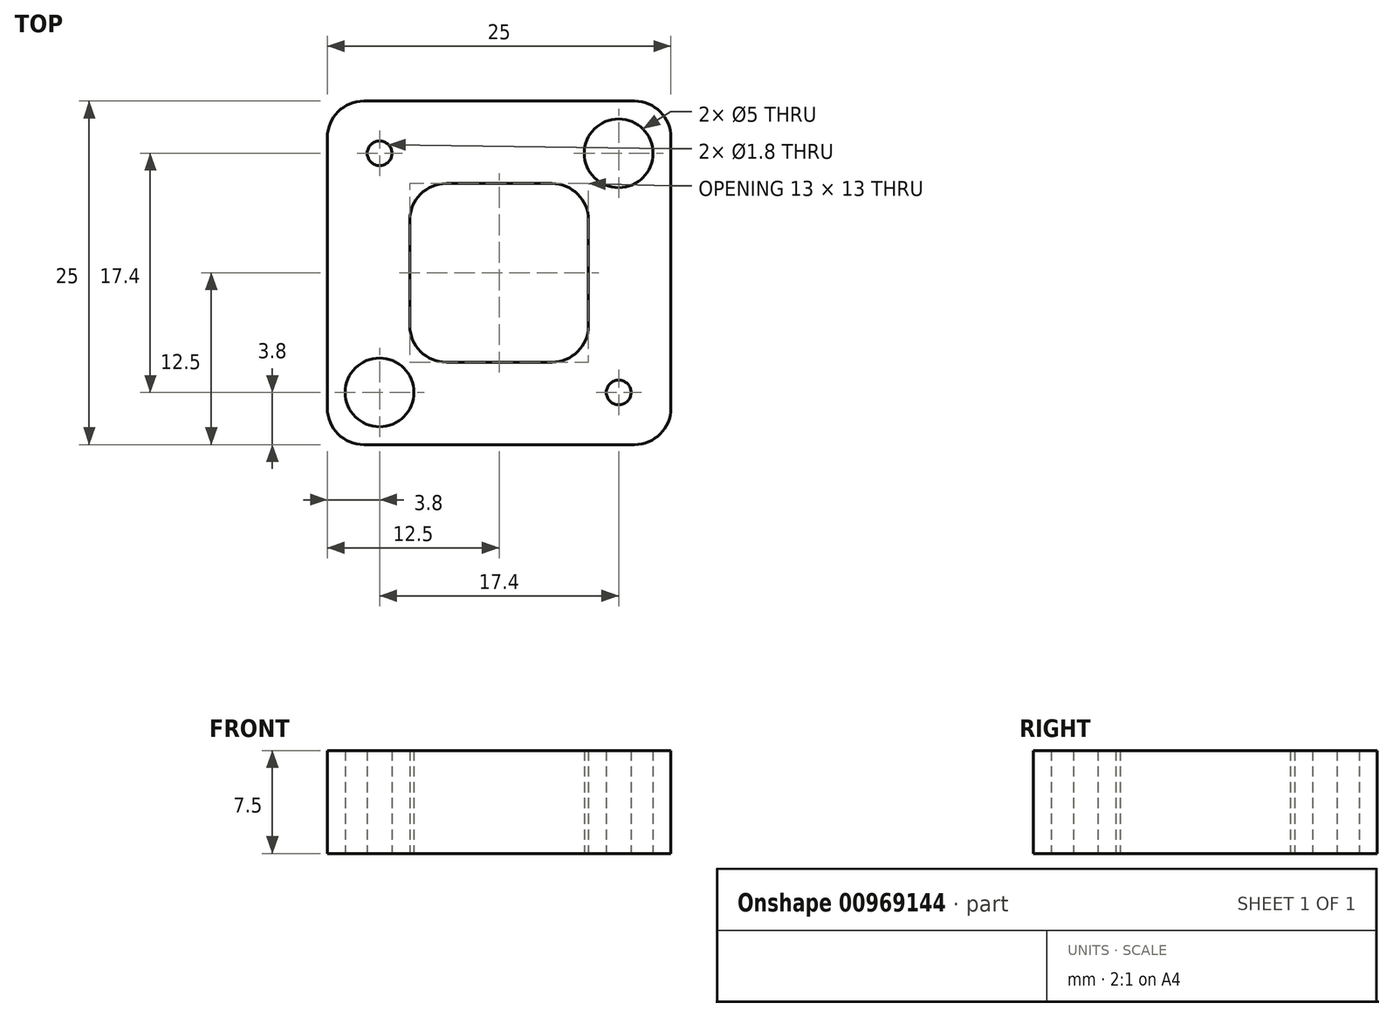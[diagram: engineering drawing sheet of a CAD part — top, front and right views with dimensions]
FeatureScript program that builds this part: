
annotation { "Feature Type Name" : "Feature", "Feature Type Description" : "" }
export const myFeature = defineFeature(function(context is Context, id is Id, definition is map)
    precondition{}
    {
        {
            var Q0;
            Q0=qCreatedBy(makeId("Top.planeOp"),FACE);
            var sketch = newSketch(context, id + "F0", { "sketchPlane" : qUnion([Q0])});
            skLineSegment(sketch, "E0.bottom", {"start": v(12.5, 12.5) * mm, "end": v(-12.5, 12.5) * mm});
            skLineSegment(sketch, "E0.top", {"start": v(12.5, -12.5) * mm, "end": v(-12.5, -12.5) * mm});
            skLineSegment(sketch, "E0.left", {"start": v(12.5, 12.5) * mm, "end": v(12.5, -12.5) * mm});
            skLineSegment(sketch, "E0.right", {"start": v(-12.5, 12.5) * mm, "end": v(-12.5, -12.5) * mm});
            skPoint(sketch, "E0.middle", {"position": v(0, 0) * mm});
            skLineSegment(sketch, "E1.bottom", {"start": v(6.5, 6.5) * mm, "end": v(-6.5, 6.5) * mm});
            skLineSegment(sketch, "E1.top", {"start": v(6.5, -6.5) * mm, "end": v(-6.5, -6.5) * mm});
            skLineSegment(sketch, "E1.left", {"start": v(6.5, 6.5) * mm, "end": v(6.5, -6.5) * mm});
            skLineSegment(sketch, "E1.right", {"start": v(-6.5, 6.5) * mm, "end": v(-6.5, -6.5) * mm});
            skCircle(sketch, "E2", {"center": v(-8.7, 8.7) * mm, "radius": 0.9 * mm});
            skCircle(sketch, "E3", {"center": v(-8.7, 8.7) * mm, "radius": 2.5 * mm});
            skLineSegment(sketch, "E4", {"start": v(-12.5, 12.5) * mm, "end": v(-6.5, 6.5) * mm, "construction": true});
            skCircle(sketch, "E5.MirrorC", {"center": v(8.7, 8.7) * mm, "radius": 2.5 * mm});
            skCircle(sketch, "E6.MirrorC", {"center": v(8.7, 8.7) * mm, "radius": 0.9 * mm});
            skCircle(sketch, "E7.MirrorC", {"center": v(8.7, -8.7) * mm, "radius": 0.9 * mm});
            skCircle(sketch, "E8.MirrorC", {"center": v(8.7, -8.7) * mm, "radius": 2.5 * mm});
            skCircle(sketch, "E9.MirrorC", {"center": v(-8.7, -8.7) * mm, "radius": 2.5 * mm});
            skCircle(sketch, "E10.MirrorC", {"center": v(-8.7, -8.7) * mm, "radius": 0.9 * mm});
            skSolve(sketch);
        }
        {
            var Q0;
            Q0=makeQuery(id+"F0.imprint","IMPRINT",FACE,{"disambiguationData":[TD([[makeQuery(id+"F0.imprint","IMPRINT",EDGE,{"derivedFrom":sQuery(id+"F0.wireOp",EDGE,"E0.bottom")}),1.0]])]});
            extrude(context, id + "F1", {"entities" : qUnion([Q0]), "depth" : 1.2 * mm, "offsetDistance" : 25 * mm});
        }
        {
            var Q0;
            Q0=makeQuery(id+"F0.imprint","IMPRINT",FACE,{"disambiguationData":[TD([[makeQuery(id+"F0.imprint","IMPRINT",EDGE,{"derivedFrom":sQuery(id+"F0.wireOp",EDGE,"E2")}),-1.0]])]});
            var Q1;
            Q1=makeQuery(id+"F0.imprint","IMPRINT",FACE,{"disambiguationData":[TD([[makeQuery(id+"F0.imprint","IMPRINT",EDGE,{"derivedFrom":sQuery(id+"F0.wireOp",EDGE,"E5.MirrorC")}),-1.0]])]});
            var Q2;
            Q2=makeQuery(id+"F0.imprint","IMPRINT",FACE,{"disambiguationData":[TD([[makeQuery(id+"F0.imprint","IMPRINT",EDGE,{"derivedFrom":sQuery(id+"F0.wireOp",EDGE,"E9.MirrorC")}),-1.0]])]});
            var Q3;
            Q3=makeQuery(id+"F0.imprint","IMPRINT",FACE,{"disambiguationData":[TD([[makeQuery(id+"F0.imprint","IMPRINT",EDGE,{"derivedFrom":sQuery(id+"F0.wireOp",EDGE,"E7.MirrorC")}),-1.0]])]});
            extrude(context, id + "F2", {"entities" : qUnion([Q0, Q1, Q2, Q3]), "operationType" : NewBodyOperationType.ADD, "depth" : 7.5 * mm, "offsetDistance" : 25 * mm});
        }
        {
            var Q0;
            Q0=makeQuery(id+"F1.opExtrude","SWEPT_EDGE",EDGE,{"disambiguationData":[OSD([sQuery(id+"F0.wireOp",EDGE,"E0.top"),sQuery(id+"F0.wireOp",EDGE,"E0.left")])]});
            var Q1;
            Q1=makeQuery(id+"F1.opExtrude","SWEPT_EDGE",EDGE,{"disambiguationData":[OSD([sQuery(id+"F0.wireOp",EDGE,"E0.bottom"),sQuery(id+"F0.wireOp",EDGE,"E0.left")])]});
            var Q2;
            Q2=makeQuery(id+"F1.opExtrude","SWEPT_EDGE",EDGE,{"disambiguationData":[OSD([sQuery(id+"F0.wireOp",EDGE,"E0.bottom"),sQuery(id+"F0.wireOp",EDGE,"E0.right")])]});
            var Q3;
            Q3=makeQuery(id+"F1.opExtrude","SWEPT_EDGE",EDGE,{"disambiguationData":[OSD([sQuery(id+"F0.wireOp",EDGE,"E0.top"),sQuery(id+"F0.wireOp",EDGE,"E0.right")])]});
            var Q4;
            Q4=makeQuery(id+"F1.opExtrude","SWEPT_EDGE",EDGE,{"disambiguationData":[OSD([sQuery(id+"F0.wireOp",EDGE,"E1.bottom"),sQuery(id+"F0.wireOp",EDGE,"E1.right")])]});
            var Q5;
            Q5=makeQuery(id+"F1.opExtrude","SWEPT_EDGE",EDGE,{"disambiguationData":[OSD([sQuery(id+"F0.wireOp",EDGE,"E1.top"),sQuery(id+"F0.wireOp",EDGE,"E1.right")])]});
            var Q6;
            Q6=makeQuery(id+"F1.opExtrude","SWEPT_EDGE",EDGE,{"disambiguationData":[OSD([sQuery(id+"F0.wireOp",EDGE,"E1.top"),sQuery(id+"F0.wireOp",EDGE,"E1.left")])]});
            var Q7;
            Q7=makeQuery(id+"F1.opExtrude","SWEPT_EDGE",EDGE,{"disambiguationData":[OSD([sQuery(id+"F0.wireOp",EDGE,"E1.bottom"),sQuery(id+"F0.wireOp",EDGE,"E1.left")])]});
            fillet(context, id + "F3", {"entities" : qUnion([Q0, Q1, Q2, Q3, Q4, Q5, Q6, Q7]), "radius" : 2.66 * mm, "tangentPropagation" : true, "allowEdgeOverflow" : false});
        }
    });
